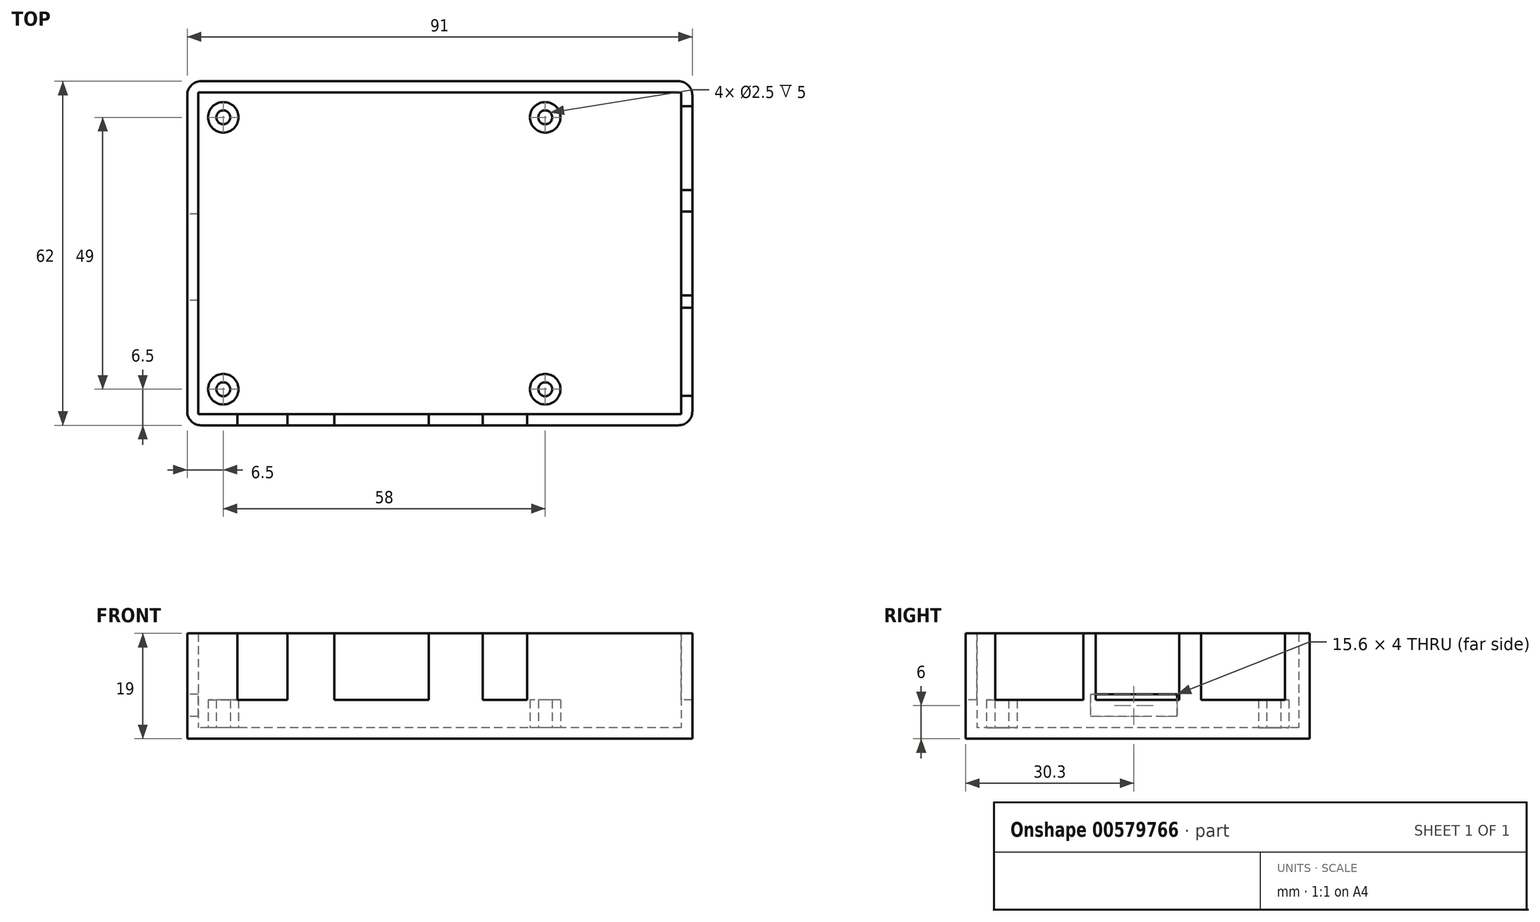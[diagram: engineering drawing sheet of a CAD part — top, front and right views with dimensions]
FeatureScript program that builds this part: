
annotation { "Feature Type Name" : "Feature", "Feature Type Description" : "" }
export const myFeature = defineFeature(function(context is Context, id is Id, definition is map)
    precondition{}
    {
        {
            var Q0;
            Q0=qCreatedBy(makeId("Top.planeOp"),FACE);
            var sketch = newSketch(context, id + "F0", { "sketchPlane" : qUnion([Q0])});
            skLineSegment(sketch, "E0.bottom", {"start": v(2.5, 0) * mm, "end": v(88.5, 0) * mm});
            skLineSegment(sketch, "E0.top", {"start": v(2.5, 62) * mm, "end": v(88.5, 62) * mm});
            skLineSegment(sketch, "E0.left", {"start": v(0, 2.5) * mm, "end": v(0, 59.5) * mm});
            skLineSegment(sketch, "E0.right", {"start": v(91, 2.5) * mm, "end": v(91, 59.5) * mm});
            skPoint(sketch, "E1.visualSharp", {"position": v(0, 62) * mm});
            skArc(sketch, "E1.filletArc", {"start": v(2.5, 62) * mm, "mid": v(0.73, 61.27) * mm, "end": v(0, 59.5) * mm});
            skPoint(sketch, "E2.visualSharp", {"position": v(91, 62) * mm});
            skArc(sketch, "E2.filletArc", {"start": v(91, 59.5) * mm, "mid": v(90.27, 61.27) * mm, "end": v(88.5, 62) * mm});
            skPoint(sketch, "E3.visualSharp", {"position": v(91, 0) * mm});
            skArc(sketch, "E3.filletArc", {"start": v(88.5, 0) * mm, "mid": v(90.27, 0.73) * mm, "end": v(91, 2.5) * mm});
            skPoint(sketch, "E4.visualSharp", {"position": v(0, 0) * mm});
            skArc(sketch, "E4.filletArc", {"start": v(0, 2.5) * mm, "mid": v(0.73, 0.73) * mm, "end": v(2.5, 0) * mm});
            skLineSegment(sketch, "E5.0", {"start": v(2, 60) * mm, "end": v(89, 60) * mm});
            skLineSegment(sketch, "E5.1", {"start": v(2, 2) * mm, "end": v(2, 60) * mm});
            skLineSegment(sketch, "E5.2", {"start": v(2, 2) * mm, "end": v(89, 2) * mm});
            skLineSegment(sketch, "E5.3", {"start": v(89, 2) * mm, "end": v(89, 60) * mm});
            skSolve(sketch);
        }
        {
            var Q0;
            Q0=makeQuery(id+"F0.imprint","IMPRINT",FACE,{"disambiguationData":[TD([[makeQuery(id+"F0.imprint","IMPRINT",EDGE,{"derivedFrom":sQuery(id+"F0.wireOp",EDGE,"E5.0")}),-1.0]])]});
            var Q1;
            Q1=makeQuery(id+"F0.imprint","IMPRINT",FACE,{"disambiguationData":[TD([[makeQuery(id+"F0.imprint","IMPRINT",EDGE,{"derivedFrom":sQuery(id+"F0.wireOp",EDGE,"E0.bottom")}),1.0]])]});
            extrude(context, id + "F1", {"entities" : qUnion([Q0, Q1]), "depth" : 2 * mm, "offsetDistance" : 25 * mm});
        }
        {
            var Q0;
            Q0 = qSketchRegion(id + "F0", true);
            extrude(context, id + "F2", {"entities" : qUnion([Q0]), "operationType" : NewBodyOperationType.ADD, "depth" : 19 * mm, "offsetDistance" : 25 * mm});
        }
        {
            var Q0;
            Q0=makeQuery(id+"F1.opExtrude","CAP_FACE",FACE,{"disambiguationData":[OSD([sQuery(id+"F0.wireOp",EDGE,"E0.bottom"),sQuery(id+"F0.wireOp",EDGE,"E0.top"),sQuery(id+"F0.wireOp",EDGE,"E0.left"),sQuery(id+"F0.wireOp",EDGE,"E0.right"),sQuery(id+"F0.wireOp",EDGE,"E1.filletArc"),sQuery(id+"F0.wireOp",EDGE,"E2.filletArc"),sQuery(id+"F0.wireOp",EDGE,"E3.filletArc"),sQuery(id+"F0.wireOp",EDGE,"E4.filletArc")])],"isStart":false});
            var sketch = newSketch(context, id + "F3", { "sketchPlane" : qUnion([Q0])});
            skCircle(sketch, "E6", {"center": v(6.5, 55.5) * mm, "radius": 2.75 * mm});
            skCircle(sketch, "E7", {"center": v(64.5, 55.5) * mm, "radius": 2.75 * mm});
            skCircle(sketch, "E8", {"center": v(6.5, 6.5) * mm, "radius": 2.75 * mm});
            skCircle(sketch, "E9", {"center": v(64.5, 6.5) * mm, "radius": 2.75 * mm});
            skCircle(sketch, "E10", {"center": v(6.5, 55.5) * mm, "radius": 1.25 * mm});
            skCircle(sketch, "E11", {"center": v(64.5, 55.5) * mm, "radius": 1.25 * mm});
            skCircle(sketch, "E12", {"center": v(64.5, 6.5) * mm, "radius": 1.25 * mm});
            skCircle(sketch, "E13", {"center": v(6.5, 6.5) * mm, "radius": 1.25 * mm});
            skSolve(sketch);
        }
        {
            var Q0;
            Q0 = qSketchRegion(id + "F3", true);
            extrude(context, id + "F4", {"entities" : qUnion([Q0]), "operationType" : NewBodyOperationType.ADD, "depth" : 5 * mm, "offsetDistance" : 25 * mm});
        }
        {
            var Q0;
            Q0=makeQuery(id+"F2.opExtrude","CAP_FACE",FACE,{"disambiguationData":[OSD([sQuery(id+"F0.wireOp",EDGE,"E0.bottom"),sQuery(id+"F0.wireOp",EDGE,"E0.top"),sQuery(id+"F0.wireOp",EDGE,"E0.left"),sQuery(id+"F0.wireOp",EDGE,"E0.right"),sQuery(id+"F0.wireOp",EDGE,"E1.filletArc"),sQuery(id+"F0.wireOp",EDGE,"E2.filletArc"),sQuery(id+"F0.wireOp",EDGE,"E3.filletArc"),sQuery(id+"F0.wireOp",EDGE,"E4.filletArc"),sQuery(id+"F0.wireOp",EDGE,"E5.0"),sQuery(id+"F0.wireOp",EDGE,"E5.1"),sQuery(id+"F0.wireOp",EDGE,"E5.2"),sQuery(id+"F0.wireOp",EDGE,"E5.3")])],"isStart":false});
            var sketch = newSketch(context, id + "F5", { "sketchPlane" : qUnion([Q0])});
            skLineSegment(sketch, "E14.bottom", {"start": v(9.05, 2) * mm, "end": v(18.05, 2) * mm});
            skLineSegment(sketch, "E14.top", {"start": v(9.05, 0) * mm, "end": v(18.05, 0) * mm});
            skLineSegment(sketch, "E14.left", {"start": v(9.05, 2) * mm, "end": v(9.05, 0) * mm});
            skLineSegment(sketch, "E14.right", {"start": v(18.05, 2) * mm, "end": v(18.05, 0) * mm});
            skLineSegment(sketch, "E15.bottom", {"start": v(53.25, 2) * mm, "end": v(61.25, 2) * mm});
            skLineSegment(sketch, "E15.top", {"start": v(53.25, 0) * mm, "end": v(61.25, 0) * mm});
            skLineSegment(sketch, "E15.left", {"start": v(53.25, 2) * mm, "end": v(53.25, 0) * mm});
            skLineSegment(sketch, "E15.right", {"start": v(61.25, 2) * mm, "end": v(61.25, 0) * mm});
            skLineSegment(sketch, "E16.bottom", {"start": v(26.5, 2) * mm, "end": v(43.5, 2) * mm});
            skLineSegment(sketch, "E16.top", {"start": v(26.5, 0) * mm, "end": v(43.5, 0) * mm});
            skLineSegment(sketch, "E16.left", {"start": v(26.5, 2) * mm, "end": v(26.5, 0) * mm});
            skLineSegment(sketch, "E16.right", {"start": v(43.5, 2) * mm, "end": v(43.5, 0) * mm});
            skLineSegment(sketch, "E17.bottom", {"start": v(91, 5.3) * mm, "end": v(89, 5.3) * mm});
            skLineSegment(sketch, "E17.top", {"start": v(91, 21.2) * mm, "end": v(89, 21.2) * mm});
            skLineSegment(sketch, "E17.left", {"start": v(91, 5.3) * mm, "end": v(91, 21.2) * mm});
            skLineSegment(sketch, "E17.right", {"start": v(89, 5.3) * mm, "end": v(89, 21.2) * mm});
            skLineSegment(sketch, "E18.bottom", {"start": v(91, 23.4) * mm, "end": v(89, 23.4) * mm});
            skLineSegment(sketch, "E18.top", {"start": v(91, 38.5) * mm, "end": v(89, 38.5) * mm});
            skLineSegment(sketch, "E18.left", {"start": v(91, 23.4) * mm, "end": v(91, 38.5) * mm});
            skLineSegment(sketch, "E18.right", {"start": v(89, 23.4) * mm, "end": v(89, 38.5) * mm});
            skLineSegment(sketch, "E19.bottom", {"start": v(91, 42.4) * mm, "end": v(89, 42.4) * mm});
            skLineSegment(sketch, "E19.top", {"start": v(91, 57.5) * mm, "end": v(89, 57.5) * mm});
            skLineSegment(sketch, "E19.left", {"start": v(91, 42.4) * mm, "end": v(91, 57.5) * mm});
            skLineSegment(sketch, "E19.right", {"start": v(89, 42.4) * mm, "end": v(89, 57.5) * mm});
            skSolve(sketch);
        }
        {
            var Q0;
            Q0 = qSketchRegion(id + "F5", true);
            extrude(context, id + "F6", {"entities" : qUnion([Q0]), "operationType" : NewBodyOperationType.REMOVE, "oppositeDirection" : true, "depth" : 12 * mm, "offsetDistance" : 25 * mm});
        }
        {
            var Q0;
            {var subQ0=sQuery(id+"F0.wireOp",EDGE,"E0.left");Q0=makeQuery(id+"F2.boolean.opBoolean","MERGE",FACE,{"derivedFrom":[makeQuery(id+"F1.opExtrude","SWEPT_FACE",FACE,{"disambiguationData":[OSD([subQ0])]}),makeQuery(id+"F2.opExtrude","SWEPT_FACE",FACE,{"disambiguationData":[OSD([subQ0])]})]});}
            var sketch = newSketch(context, id + "F7", { "sketchPlane" : qUnion([Q0])});
            skLineSegment(sketch, "E20.bottom", {"start": v(-38.1, 8) * mm, "end": v(-22.5, 8) * mm});
            skLineSegment(sketch, "E20.top", {"start": v(-38.1, 4) * mm, "end": v(-22.5, 4) * mm});
            skLineSegment(sketch, "E20.left", {"start": v(-38.1, 8) * mm, "end": v(-38.1, 4) * mm});
            skLineSegment(sketch, "E20.right", {"start": v(-22.5, 8) * mm, "end": v(-22.5, 4) * mm});
            skSolve(sketch);
        }
        {
            var Q0;
            Q0 = qSketchRegion(id + "F7", true);
            var Q1;
            {var subQ0=sQuery(id+"F0.wireOp",EDGE,"E0.left");Q1=makeQuery(id+"F2.boolean.opBoolean","MERGE",FACE,{"derivedFrom":[makeQuery(id+"F1.opExtrude","SWEPT_FACE",FACE,{"disambiguationData":[OSD([subQ0])]}),makeQuery(id+"F2.opExtrude","SWEPT_FACE",FACE,{"disambiguationData":[OSD([subQ0])]})]});}
            extrude(context, id + "F8", {"entities" : qUnion([Q0]), "operationType" : NewBodyOperationType.REMOVE, "endBound" : BoundingType.UP_TO_NEXT, "oppositeDirection" : true, "depth" : 25 * mm, "endBoundEntityFace" : qUnion([Q1]), "offsetDistance" : 25 * mm});
        }
    });
